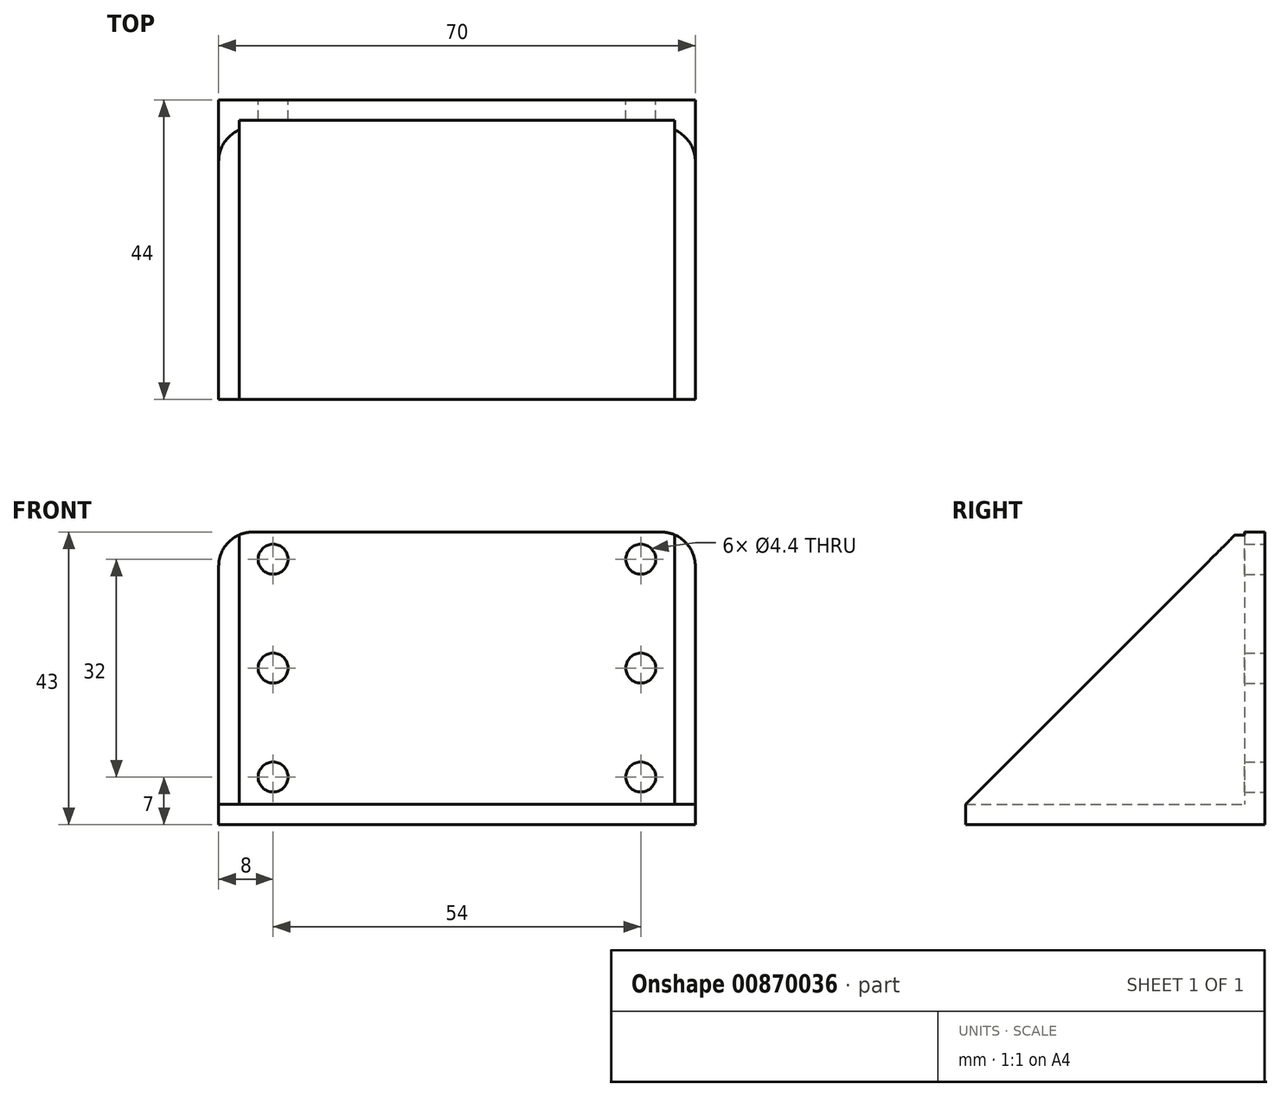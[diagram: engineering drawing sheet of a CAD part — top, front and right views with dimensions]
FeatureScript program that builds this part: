
annotation { "Feature Type Name" : "Feature", "Feature Type Description" : "" }
export const myFeature = defineFeature(function(context is Context, id is Id, definition is map)
    precondition{}
    {
        {
            var Q0;
            Q0=qCreatedBy(makeId("Front.planeOp"),FACE);
            var sketch = newSketch(context, id + "F0", { "sketchPlane" : qUnion([Q0])});
            skLineSegment(sketch, "E0.bottom", {"start": v(32, -20) * mm, "end": v(-32, -20) * mm});
            skLineSegment(sketch, "E0.top", {"start": v(32, 20) * mm, "end": v(-32, 20) * mm});
            skLineSegment(sketch, "E0.left", {"start": v(32, -20) * mm, "end": v(32, 20) * mm});
            skLineSegment(sketch, "E0.right", {"start": v(-32, -20) * mm, "end": v(-32, 20) * mm});
            skPoint(sketch, "E0.middle", {"position": v(0, 0) * mm});
            skCircle(sketch, "E1", {"center": v(-27, 0) * mm, "radius": 2.2 * mm});
            skLineSegment(sketch, "E2", {"start": v(-27, -20) * mm, "end": v(-27, 20) * mm, "construction": true});
            skCircle(sketch, "E3", {"center": v(-27, 16) * mm, "radius": 2.2 * mm});
            skCircle(sketch, "E4.MirrorC", {"center": v(-27, -16) * mm, "radius": 2.2 * mm});
            skCircle(sketch, "E5.MirrorC", {"center": v(27, 16) * mm, "radius": 2.2 * mm});
            skCircle(sketch, "E6.MirrorC", {"center": v(27, 0) * mm, "radius": 2.2 * mm});
            skCircle(sketch, "E7.MirrorC", {"center": v(27, -16) * mm, "radius": 2.2 * mm});
            skLineSegment(sketch, "E8.bottom", {"start": v(-32, -20) * mm, "end": v(32, -20) * mm});
            skLineSegment(sketch, "E8.top", {"start": v(-32, -23) * mm, "end": v(32, -23) * mm});
            skLineSegment(sketch, "E8.left", {"start": v(-32, -20) * mm, "end": v(-32, -23) * mm});
            skLineSegment(sketch, "E8.right", {"start": v(32, -20) * mm, "end": v(32, -23) * mm});
            skLineSegment(sketch, "E9.bottom", {"start": v(-32, 20) * mm, "end": v(-35, 20) * mm});
            skLineSegment(sketch, "E9.top", {"start": v(-32, -23) * mm, "end": v(-35, -23) * mm});
            skLineSegment(sketch, "E9.left", {"start": v(-32, 20) * mm, "end": v(-32, -23) * mm});
            skLineSegment(sketch, "E9.right", {"start": v(-35, 20) * mm, "end": v(-35, -23) * mm});
            skLineSegment(sketch, "E10.bottom", {"start": v(32, 20) * mm, "end": v(35, 20) * mm});
            skLineSegment(sketch, "E10.top", {"start": v(32, -23) * mm, "end": v(35, -23) * mm});
            skLineSegment(sketch, "E10.left", {"start": v(32, 20) * mm, "end": v(32, -23) * mm});
            skLineSegment(sketch, "E10.right", {"start": v(35, 20) * mm, "end": v(35, -23) * mm});
            skSolve(sketch);
        }
        {
            var Q0;
            {var subQ0=makeQuery(id+"F0.imprint","IMPRINT",EDGE,{"derivedFrom":sQuery(id+"F0.wireOp",EDGE,"E0.bottom")});var subQ3=makeQuery(id+"F0.imprint","IMPRINT",EDGE,{"derivedFrom":sQuery(id+"F0.wireOp",EDGE,"E0.right")});var subQ4=makeQuery(id+"F0.imprint","IMPRINT",EDGE,{"derivedFrom":sQuery(id+"F0.wireOp",EDGE,"E0.left")});Q0=qUnion([makeQuery(id+"F0.imprint","IMPRINT",FACE,{"disambiguationData":[TD([[subQ0,-1.0]])]}),makeQuery(id+"F0.imprint","IMPRINT",FACE,{"disambiguationData":[TD([[subQ4,-1.0]])]}),makeQuery(id+"F0.imprint","IMPRINT",FACE,{"disambiguationData":[TD([[subQ3,1.0]])]}),makeQuery(id+"F0.imprint","IMPRINT",FACE,{"disambiguationData":[TD([[subQ0,1.0]])]})]);}
            extrude(context, id + "F1", {"entities" : qUnion([Q0]), "depth" : 3 * mm, "offsetDistance" : 25 * mm});
        }
        {
            var Q0;
            Q0=makeQuery(id+"F0.imprint","IMPRINT",FACE,{"disambiguationData":[TD([[makeQuery(id+"F0.imprint","IMPRINT",EDGE,{"derivedFrom":sQuery(id+"F0.wireOp",EDGE,"E0.bottom")}),1.0]])]});
            var Q1;
            Q1=makeQuery(id+"F0.imprint","IMPRINT",FACE,{"disambiguationData":[TD([[makeQuery(id+"F0.imprint","IMPRINT",EDGE,{"derivedFrom":sQuery(id+"F0.wireOp",EDGE,"E0.left")}),-1.0]])]});
            var Q2;
            Q2=makeQuery(id+"F0.imprint","IMPRINT",FACE,{"disambiguationData":[TD([[makeQuery(id+"F0.imprint","IMPRINT",EDGE,{"derivedFrom":sQuery(id+"F0.wireOp",EDGE,"E0.right")}),1.0]])]});
            extrude(context, id + "F2", {"entities" : qUnion([Q0, Q1, Q2]), "operationType" : NewBodyOperationType.ADD, "depth" : 44 * mm, "offsetDistance" : 25 * mm});
        }
        {
            var Q0;
            Q0=makeQuery(id+"F2.opExtrude","CAP_EDGE",EDGE,{"disambiguationData":[OSD([sQuery(id+"F0.wireOp",EDGE,"E9.bottom")])],"isStart":false});
            var Q1;
            Q1=makeQuery(id+"F2.opExtrude","CAP_EDGE",EDGE,{"disambiguationData":[OSD([sQuery(id+"F0.wireOp",EDGE,"E10.bottom")])],"isStart":false});
            chamfer(context, id + "F3", {"entities" : qUnion([Q0, Q1]), "width" : 40 * mm, "tangentPropagation" : true});
        }
        {
            var Q0;
            {var subQ0=sQuery(id+"F0.wireOp",EDGE,"E10.right");var subQ1=sQuery(id+"F0.wireOp",EDGE,"E10.bottom");Q0=makeQuery(id+"F2.boolean.opBoolean","MERGE",EDGE,{"derivedFrom":[makeQuery(id+"F1.opExtrude","SWEPT_EDGE",EDGE,{"disambiguationData":[OSD([subQ1,subQ0])]}),makeQuery(id+"F2.opExtrude","SWEPT_EDGE",EDGE,{"disambiguationData":[OSD([subQ1,subQ0])]})]});}
            var Q1;
            {var subQ0=sQuery(id+"F0.wireOp",EDGE,"E9.right");var subQ1=sQuery(id+"F0.wireOp",EDGE,"E9.bottom");Q1=makeQuery(id+"F2.boolean.opBoolean","MERGE",EDGE,{"derivedFrom":[makeQuery(id+"F1.opExtrude","SWEPT_EDGE",EDGE,{"disambiguationData":[OSD([subQ1,subQ0])]}),makeQuery(id+"F2.opExtrude","SWEPT_EDGE",EDGE,{"disambiguationData":[OSD([subQ1,subQ0])]})]});}
            fillet(context, id + "F4", {"entities" : qUnion([Q0, Q1]), "radius" : 5 * mm, "tangentPropagation" : true, "allowEdgeOverflow" : false});
        }
    });
